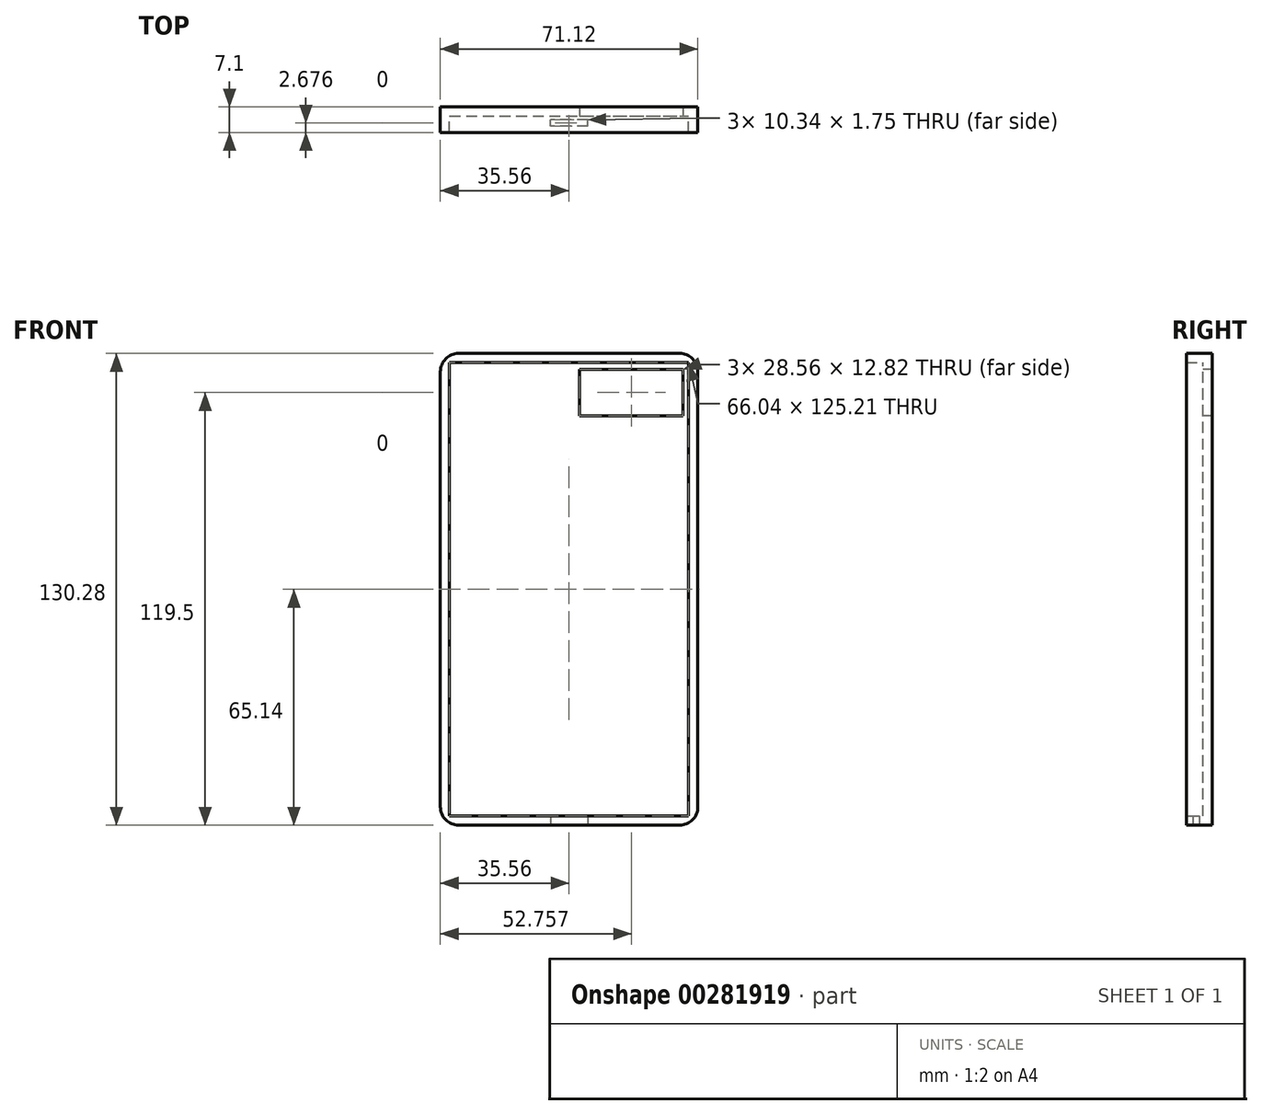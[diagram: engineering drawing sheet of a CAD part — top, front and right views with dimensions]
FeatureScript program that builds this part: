
annotation { "Feature Type Name" : "Feature", "Feature Type Description" : "" }
export const myFeature = defineFeature(function(context is Context, id is Id, definition is map)
    precondition{}
    {
        {
            var Q0;
            Q0=qCreatedBy(makeId("Front.planeOp"),FACE);
            var sketch = newSketch(context, id + "F0", { "sketchPlane" : qUnion([Q0])});
            skLineSegment(sketch, "E0.bottom", {"start": v(-35.56, -65.14) * mm, "end": v(35.56, -65.14) * mm});
            skLineSegment(sketch, "E0.top", {"start": v(-35.56, 65.14) * mm, "end": v(35.56, 65.14) * mm});
            skLineSegment(sketch, "E0.left", {"start": v(-35.56, -65.14) * mm, "end": v(-35.56, 65.14) * mm});
            skLineSegment(sketch, "E0.right", {"start": v(35.56, -65.14) * mm, "end": v(35.56, 65.14) * mm});
            skPoint(sketch, "E0.middle", {"position": v(0, 0) * mm});
            skSolve(sketch);
        }
        {
            var Q0;
            Q0=makeQuery(id+"F0.imprint","IMPRINT",FACE,{"disambiguationData":[TD([[makeQuery(id+"F0.imprint","IMPRINT",EDGE,{"derivedFrom":sQuery(id+"F0.wireOp",EDGE,"E0.bottom")}),1.0]])]});
            extrude(context, id + "F1", {"entities" : qUnion([Q0]), "endBound" : BoundingType.SYMMETRIC, "depth" : 7.1 * mm});
        }
        {
            var Q0;
            Q0=makeQuery(id+"F1.opExtrude","CAP_FACE",FACE,{"disambiguationData":[OSD([sQuery(id+"F0.wireOp",EDGE,"E0.bottom"),sQuery(id+"F0.wireOp",EDGE,"E0.top"),sQuery(id+"F0.wireOp",EDGE,"E0.left"),sQuery(id+"F0.wireOp",EDGE,"E0.right")])],"isStart":false});
            shell(context, id + "F2", {"entities" : qUnion([Q0]), "thickness" : 2.54 * mm});
        }
        {
            var Q0;
            Q0=makeQuery(id+"F1.opExtrude","SWEPT_EDGE",EDGE,{"disambiguationData":[OSD([sQuery(id+"F0.wireOp",EDGE,"E0.top"),sQuery(id+"F0.wireOp",EDGE,"E0.right")])]});
            var Q1;
            Q1=makeQuery(id+"F1.opExtrude","SWEPT_EDGE",EDGE,{"disambiguationData":[OSD([sQuery(id+"F0.wireOp",EDGE,"E0.top"),sQuery(id+"F0.wireOp",EDGE,"E0.left")])]});
            var Q2;
            Q2=makeQuery(id+"F1.opExtrude","SWEPT_EDGE",EDGE,{"disambiguationData":[OSD([sQuery(id+"F0.wireOp",EDGE,"E0.bottom"),sQuery(id+"F0.wireOp",EDGE,"E0.right")])]});
            var Q3;
            Q3=makeQuery(id+"F1.opExtrude","SWEPT_EDGE",EDGE,{"disambiguationData":[OSD([sQuery(id+"F0.wireOp",EDGE,"E0.bottom"),sQuery(id+"F0.wireOp",EDGE,"E0.left")])]});
            fillet(context, id + "F3", {"entities" : qUnion([Q0, Q1, Q2, Q3]), "radius" : 5.08 * mm, "tangentPropagation" : true, "allowEdgeOverflow" : false});
        }
        {
            var Q0;
            Q0=makeQuery(id+"F2.opShell","OFFSET_FACE",FACE,{"disambiguationData":[OSD([sQuery(id+"F0.wireOp",EDGE,"E0.bottom"),sQuery(id+"F0.wireOp",EDGE,"E0.top"),sQuery(id+"F0.wireOp",EDGE,"E0.left"),sQuery(id+"F0.wireOp",EDGE,"E0.right")])]});
            var sketch = newSketch(context, id + "F4", { "sketchPlane" : qUnion([Q0])});
            skLineSegment(sketch, "E1.bottom", {"start": v(2.91, 47.95) * mm, "end": v(31.48, 47.95) * mm});
            skLineSegment(sketch, "E1.top", {"start": v(2.91, 60.77) * mm, "end": v(31.48, 60.77) * mm});
            skLineSegment(sketch, "E1.left", {"start": v(2.91, 47.95) * mm, "end": v(2.91, 60.77) * mm});
            skLineSegment(sketch, "E1.right", {"start": v(31.48, 47.95) * mm, "end": v(31.48, 60.77) * mm});
            skPoint(sketch, "E1.middle", {"position": v(17.2, 54.36) * mm});
            skSolve(sketch);
        }
        {
            var Q0;
            Q0=makeQuery(id+"F4.imprint","IMPRINT",FACE,{"disambiguationData":[TD([[makeQuery(id+"F4.imprint","IMPRINT",EDGE,{"derivedFrom":sQuery(id+"F4.wireOp",EDGE,"E1.bottom")}),1.0]])]});
            extrude(context, id + "F5", {"entities" : qUnion([Q0]), "operationType" : NewBodyOperationType.REMOVE, "endBound" : BoundingType.SYMMETRIC, "oppositeDirection" : true, "depth" : 25 * mm});
        }
        {
            var Q0;
            Q0=makeQuery(id+"F1.opExtrude","SWEPT_FACE",FACE,{"disambiguationData":[OSD([sQuery(id+"F0.wireOp",EDGE,"E0.bottom")])]});
            var sketch = newSketch(context, id + "F6", { "sketchPlane" : qUnion([Q0])});
            skLineSegment(sketch, "E2.bottom", {"start": v(-5.17, 0) * mm, "end": v(5.17, 0) * mm});
            skLineSegment(sketch, "E2.top", {"start": v(-5.17, 1.75) * mm, "end": v(5.17, 1.75) * mm});
            skLineSegment(sketch, "E2.left", {"start": v(-5.17, 0) * mm, "end": v(-5.17, 1.75) * mm});
            skLineSegment(sketch, "E2.right", {"start": v(5.17, 0) * mm, "end": v(5.17, 1.75) * mm});
            skPoint(sketch, "E2.middle", {"position": v(0, 0.87) * mm});
            skSolve(sketch);
        }
        {
            var Q0;
            Q0=makeQuery(id+"F6.imprint","IMPRINT",FACE,{"disambiguationData":[TD([[makeQuery(id+"F6.imprint","IMPRINT",EDGE,{"derivedFrom":sQuery(id+"F6.wireOp",EDGE,"E2.bottom")}),1.0]])]});
            extrude(context, id + "F7", {"entities" : qUnion([Q0]), "operationType" : NewBodyOperationType.REMOVE, "endBound" : BoundingType.SYMMETRIC, "oppositeDirection" : true, "depth" : 25 * mm});
        }
    });
